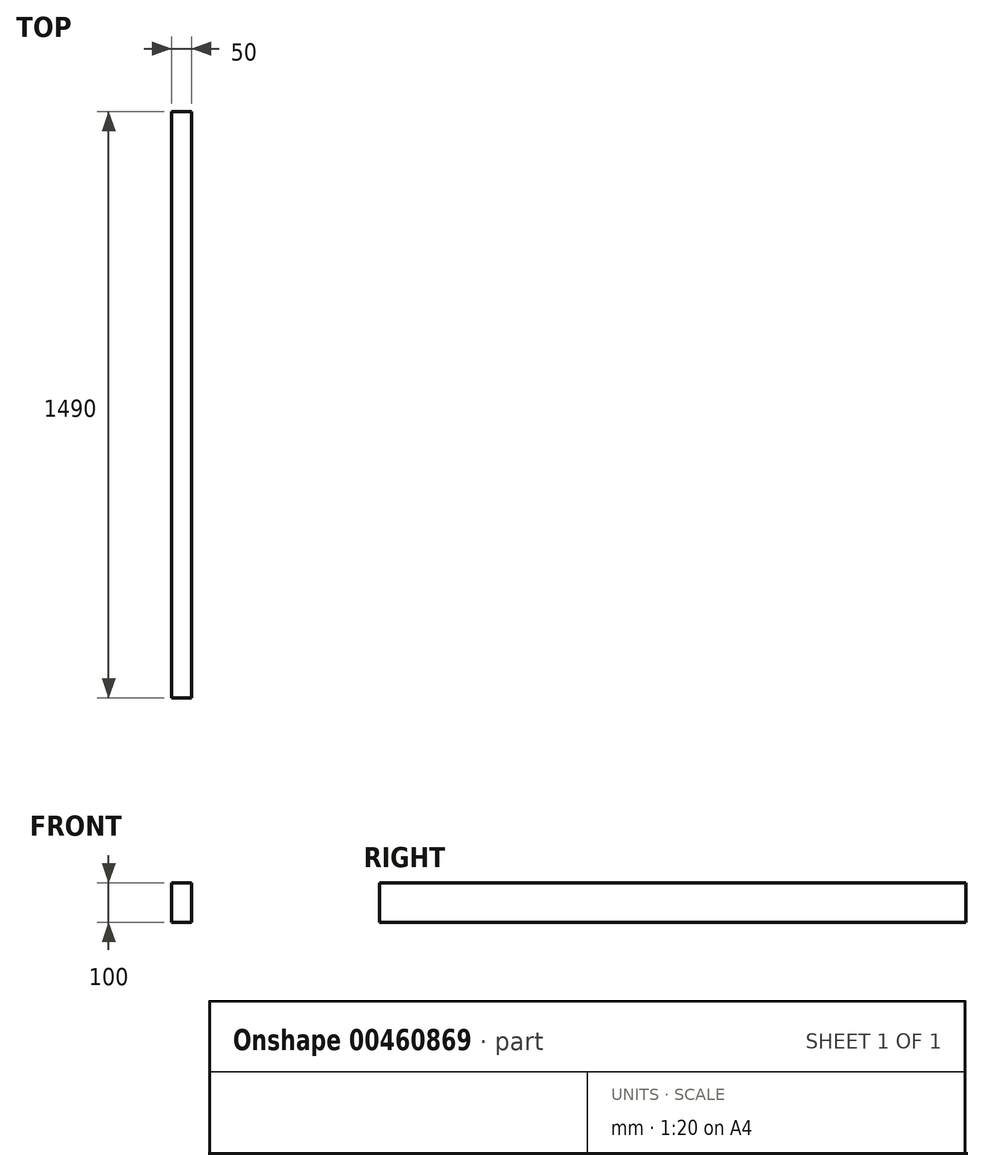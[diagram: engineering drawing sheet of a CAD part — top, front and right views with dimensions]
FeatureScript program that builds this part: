
annotation { "Feature Type Name" : "Feature", "Feature Type Description" : "" }
export const myFeature = defineFeature(function(context is Context, id is Id, definition is map)
    precondition{}
    {
        {
            var Q0;
            Q0=qCreatedBy(makeId("Front.planeOp"),FACE);
            var sketch = newSketch(context, id + "F0", { "sketchPlane" : qUnion([Q0])});
            skLineSegment(sketch, "E0.bottom", {"start": v(31.76, 21.1) * mm, "end": v(81.76, 21.1) * mm});
            skLineSegment(sketch, "E0.top", {"start": v(31.76, 121.1) * mm, "end": v(81.76, 121.1) * mm});
            skLineSegment(sketch, "E0.left", {"start": v(31.76, 21.1) * mm, "end": v(31.76, 121.1) * mm});
            skLineSegment(sketch, "E0.right", {"start": v(81.76, 21.1) * mm, "end": v(81.76, 121.1) * mm});
            skSolve(sketch);
        }
        {
            var Q0;
            Q0=qSketchRegion(id+"F0",true);
            extrude(context, id + "F1", {"entities" : qUnion([Q0]), "oppositeDirection" : true, "depth" : 1490 * mm});
        }
    });
